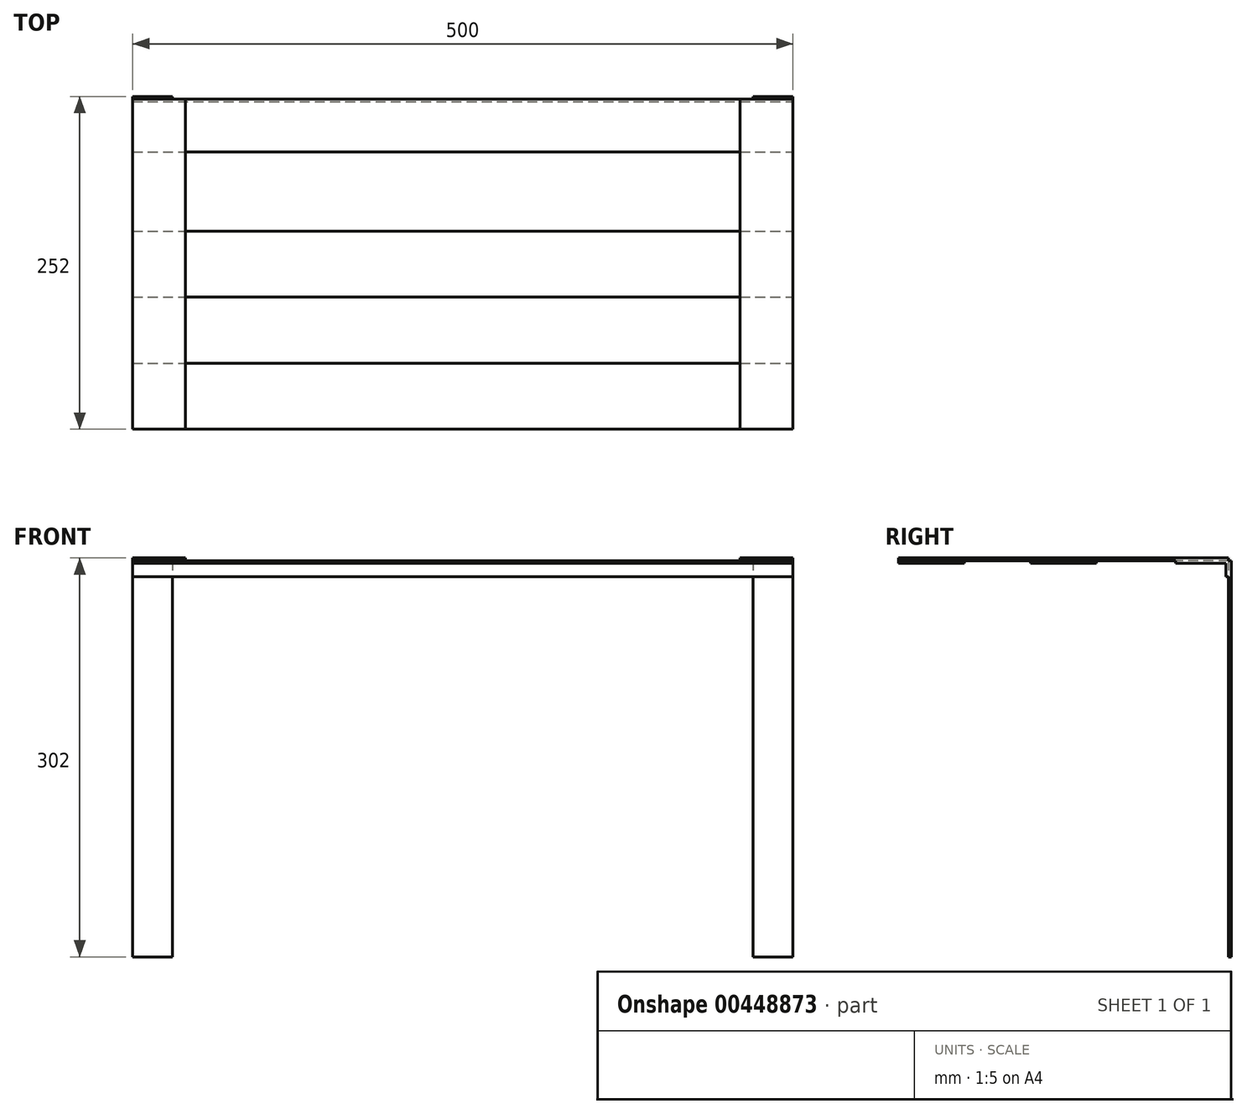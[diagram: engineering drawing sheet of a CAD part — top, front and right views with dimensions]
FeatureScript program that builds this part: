
annotation { "Feature Type Name" : "Feature", "Feature Type Description" : "" }
export const myFeature = defineFeature(function(context is Context, id is Id, definition is map)
    precondition{}
    {
        {
            var Q0;
            Q0=qCreatedBy(makeId("Top.planeOp"),FACE);
            var sketch = newSketch(context, id + "F0", { "sketchPlane" : qUnion([Q0])});
            skLineSegment(sketch, "E0.bottom", {"start": v(-251.12, 227.53) * mm, "end": v(248.88, 227.53) * mm});
            skLineSegment(sketch, "E0.top", {"start": v(-251.12, 187.53) * mm, "end": v(248.88, 187.53) * mm});
            skLineSegment(sketch, "E0.left", {"start": v(-251.12, 227.53) * mm, "end": v(-251.12, 187.53) * mm});
            skLineSegment(sketch, "E0.right", {"start": v(248.88, 227.53) * mm, "end": v(248.88, 187.53) * mm});
            skSolve(sketch);
        }
        {
            var Q0;
            Q0=makeQuery(id+"F0.imprint","IMPRINT",FACE,{"disambiguationData":[TD([[makeQuery(id+"F0.imprint","IMPRINT",EDGE,{"derivedFrom":sQuery(id+"F0.wireOp",EDGE,"E0.bottom")}),-1.0]])]});
            var Q1;
            Q1=makeQuery(id+"F0.imprint","IMPRINT",FACE,{"disambiguationData":[TD([[makeQuery(id+"F0.imprint","IMPRINT",EDGE,{"derivedFrom":sQuery(id+"F0.wireOp",EDGE,"f7a62b93-0d42-4e9c-ae8b-a5ed1b1f8d5c.bottom")}),-1.0]])]});
            extrude(context, id + "F1", {"entities" : qUnion([Q0, Q1]), "oppositeDirection" : true, "depth" : 2 * mm});
        }
        {
            var Q0;
            Q0=qCreatedBy(makeId("Top.planeOp"),FACE);
            var sketch = newSketch(context, id + "F2", { "sketchPlane" : qUnion([Q0])});
            skLineSegment(sketch, "E1.bottom", {"start": v(-251.12, -22.47) * mm, "end": v(-211.12, -22.47) * mm});
            skLineSegment(sketch, "E1.top", {"start": v(-251.12, 227.53) * mm, "end": v(-211.12, 227.53) * mm});
            skLineSegment(sketch, "E1.left", {"start": v(-251.12, 227.53) * mm, "end": v(-251.12, -22.47) * mm});
            skLineSegment(sketch, "E1.right", {"start": v(-211.12, 227.53) * mm, "end": v(-211.12, -22.47) * mm});
            skLineSegment(sketch, "E2.bottom", {"start": v(248.88, -22.47) * mm, "end": v(208.88, -22.47) * mm});
            skLineSegment(sketch, "E2.top", {"start": v(248.88, 227.53) * mm, "end": v(208.88, 227.53) * mm});
            skLineSegment(sketch, "E2.left", {"start": v(248.88, 227.53) * mm, "end": v(248.88, -22.47) * mm});
            skLineSegment(sketch, "E2.right", {"start": v(208.88, 227.53) * mm, "end": v(208.88, -22.47) * mm});
            skSolve(sketch);
        }
        {
            var Q0;
            Q0 = qSketchRegion(id + "F2", true);
            extrude(context, id + "F3", {"entities" : qUnion([Q0]), "depth" : 2 * mm});
        }
        {
            var Q0;
            Q0=qCreatedBy(makeId("Top.planeOp"),FACE);
            var sketch = newSketch(context, id + "F4", { "sketchPlane" : qUnion([Q0])});
            skLineSegment(sketch, "E3.bottom", {"start": v(-251.12, -22.47) * mm, "end": v(248.88, -22.47) * mm});
            skLineSegment(sketch, "E3.top", {"start": v(-251.12, 27.53) * mm, "end": v(248.88, 27.53) * mm});
            skLineSegment(sketch, "E3.left", {"start": v(-251.12, -22.47) * mm, "end": v(-251.12, 27.53) * mm});
            skLineSegment(sketch, "E3.right", {"start": v(248.88, -22.47) * mm, "end": v(248.88, 27.53) * mm});
            skLineSegment(sketch, "E4", {"start": v(290.3, 102.53) * mm, "end": v(-351.33, 102.53) * mm, "construction": true});
            skLineSegment(sketch, "E5.0.1.0", {"start": v(-251.12, 127.53) * mm, "end": v(248.88, 127.53) * mm});
            skLineSegment(sketch, "E5.0.1.1", {"start": v(-251.12, 77.53) * mm, "end": v(-251.12, 127.53) * mm});
            skLineSegment(sketch, "E5.0.1.2", {"start": v(-251.12, 77.53) * mm, "end": v(248.88, 77.53) * mm});
            skLineSegment(sketch, "E5.0.1.3", {"start": v(248.88, 77.53) * mm, "end": v(248.88, 127.53) * mm});
            skLineSegment(sketch, "E5.direction1", {"start": v(-251.12, -22.47) * mm, "end": v(-226.12, -22.47) * mm, "construction": true});
            skLineSegment(sketch, "E5.direction2", {"start": v(-251.12, -22.47) * mm, "end": v(-251.12, 77.53) * mm, "construction": true});
            skSolve(sketch);
        }
        {
            var Q0;
            Q0 = qSketchRegion(id + "F4", true);
            extrude(context, id + "F5", {"entities" : qUnion([Q0]), "oppositeDirection" : true, "depth" : 2 * mm});
        }
        {
            var Q0;
            Q0=qCreatedBy(makeId("Top.planeOp"),FACE);
            var sketch = newSketch(context, id + "F6", { "sketchPlane" : qUnion([Q0])});
            skLineSegment(sketch, "E6.bottom", {"start": v(-251.12, 227.53) * mm, "end": v(248.88, 227.53) * mm, "construction": true});
            skLineSegment(sketch, "E6.top", {"start": v(-251.12, -122.47) * mm, "end": v(248.88, -122.47) * mm, "construction": true});
            skLineSegment(sketch, "E6.left", {"start": v(-251.12, 227.53) * mm, "end": v(-251.12, -122.47) * mm, "construction": true});
            skLineSegment(sketch, "E6.right", {"start": v(248.88, 227.53) * mm, "end": v(248.88, -122.47) * mm, "construction": true});
            skSolve(sketch);
        }
        {
            var Q0;
            Q0=makeQuery(id+"F1.opExtrude","CAP_FACE",FACE,{"disambiguationData":[OSD([sQuery(id+"F0.wireOp",EDGE,"E0.bottom"),sQuery(id+"F0.wireOp",EDGE,"E0.top"),sQuery(id+"F0.wireOp",EDGE,"E0.left"),sQuery(id+"F0.wireOp",EDGE,"E0.right")])],"isStart":false});
            var sketch = newSketch(context, id + "F7", { "sketchPlane" : qUnion([Q0])});
            skLineSegment(sketch, "E7.bottom", {"start": v(-251.12, -227.53) * mm, "end": v(248.88, -227.53) * mm});
            skLineSegment(sketch, "E7.top", {"start": v(-251.12, -225.53) * mm, "end": v(248.88, -225.53) * mm});
            skLineSegment(sketch, "E7.left", {"start": v(-251.12, -227.53) * mm, "end": v(-251.12, -225.53) * mm});
            skLineSegment(sketch, "E7.right", {"start": v(248.88, -227.53) * mm, "end": v(248.88, -225.53) * mm});
            skSolve(sketch);
        }
        {
            var Q0;
            Q0 = qSketchRegion(id + "F7", true);
            extrude(context, id + "F8", {"entities" : qUnion([Q0]), "operationType" : NewBodyOperationType.ADD, "depth" : 10 * mm});
        }
        {
            var Q0;
            Q0=makeQuery(id+"F8.boolean.opBoolean","MERGE",FACE,{"derivedFrom":[makeQuery(id+"F1.opExtrude","SWEPT_FACE",FACE,{"disambiguationData":[OSD([sQuery(id+"F0.wireOp",EDGE,"E0.bottom")])]}),makeQuery(id+"F8.opExtrude","SWEPT_FACE",FACE,{"disambiguationData":[OSD([sQuery(id+"F7.wireOp",EDGE,"E7.bottom")])]})]});
            var sketch = newSketch(context, id + "F9", { "sketchPlane" : qUnion([Q0])});
            skLineSegment(sketch, "E8.bottom", {"start": v(-248.88, 0) * mm, "end": v(-218.88, 0) * mm});
            skLineSegment(sketch, "E8.top", {"start": v(-248.88, -300) * mm, "end": v(-218.88, -300) * mm});
            skLineSegment(sketch, "E8.left", {"start": v(-248.88, 0) * mm, "end": v(-248.88, -300) * mm});
            skLineSegment(sketch, "E8.right", {"start": v(-218.88, 0) * mm, "end": v(-218.88, -300) * mm});
            skLineSegment(sketch, "E9.bottom", {"start": v(221.12, 0) * mm, "end": v(251.12, 0) * mm});
            skLineSegment(sketch, "E9.top", {"start": v(221.12, -300) * mm, "end": v(251.12, -300) * mm});
            skLineSegment(sketch, "E9.left", {"start": v(221.12, 0) * mm, "end": v(221.12, -300) * mm});
            skLineSegment(sketch, "E9.right", {"start": v(251.12, 0) * mm, "end": v(251.12, -300) * mm});
            skSolve(sketch);
        }
        {
            var Q0;
            Q0 = qSketchRegion(id + "F9", true);
            extrude(context, id + "F10", {"entities" : qUnion([Q0]), "operationType" : NewBodyOperationType.ADD, "depth" : 2 * mm});
        }
    });
